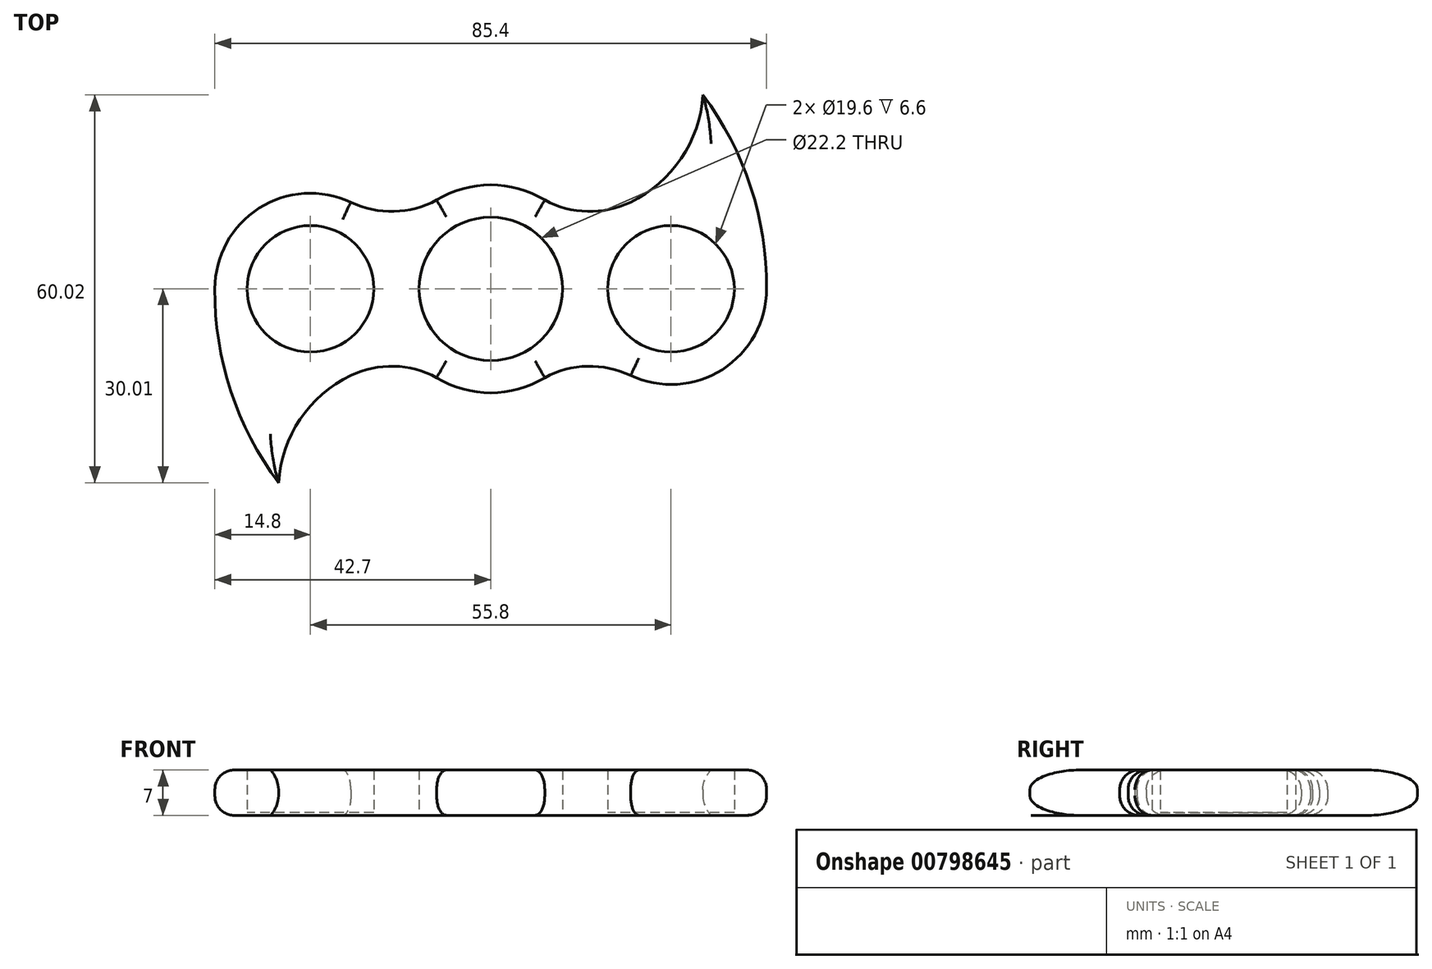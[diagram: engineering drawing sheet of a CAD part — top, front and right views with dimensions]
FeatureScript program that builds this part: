
annotation { "Feature Type Name" : "Feature", "Feature Type Description" : "" }
export const myFeature = defineFeature(function(context is Context, id is Id, definition is map)
    precondition{}
    {
        {
            var Q0;
            Q0=qCreatedBy(makeId("Top.planeOp"),FACE);
            var sketch = newSketch(context, id + "F0", { "sketchPlane" : qUnion([Q0])});
            skCircle(sketch, "E0", {"center": v(0, 0) * mm, "radius": 11.1 * mm});
            skCircle(sketch, "E1", {"center": v(27.9, 0) * mm, "radius": 9.8 * mm});
            skPoint(sketch, "E2", {"position": v(11.1, 0) * mm});
            skPoint(sketch, "E3", {"position": v(18.1, 0) * mm});
            skArc(sketch, "E4.0", {"start": v(21.5, -13.35) * mm, "mid": v(35.79, -12.52) * mm, "end": v(42.7, 0) * mm});
            skArc(sketch, "E5.0", {"start": v(-8.37, -13.76) * mm, "mid": v(0, -16.1) * mm, "end": v(8.37, -13.76) * mm});
            skArc(sketch, "E6", {"start": v(8.37, 13.76) * mm, "mid": v(14.97, 11.99) * mm, "end": v(21.65, 13.42) * mm});
            skArc(sketch, "E7", {"start": v(21.65, 13.42) * mm, "mid": v(29.5, 20.2) * mm, "end": v(32.85, 30.01) * mm});
            skArc(sketch, "E8", {"start": v(42.7, 0) * mm, "mid": v(40.23, 15.81) * mm, "end": v(32.85, 30.01) * mm});
            skArc(sketch, "E9.MirrorCS", {"start": v(8.37, -13.76) * mm, "mid": v(14.97, -11.99) * mm, "end": v(21.65, -13.42) * mm});
            skCircle(sketch, "E10.1.0", {"center": v(-27.9, 0) * mm, "radius": 9.8 * mm});
            skArc(sketch, "E10.1.1", {"start": v(-21.5, 13.35) * mm, "mid": v(-35.79, 12.52) * mm, "end": v(-42.7, 0) * mm});
            skArc(sketch, "E10.1.2", {"start": v(-42.7, 0) * mm, "mid": v(-40.23, -15.81) * mm, "end": v(-32.85, -30.01) * mm});
            skArc(sketch, "E10.1.3", {"start": v(-21.65, -13.42) * mm, "mid": v(-29.5, -20.2) * mm, "end": v(-32.85, -30.01) * mm});
            skArc(sketch, "E10.1.4", {"start": v(-8.37, -13.76) * mm, "mid": v(-14.97, -11.99) * mm, "end": v(-21.65, -13.42) * mm});
            skArc(sketch, "E10.1.5", {"start": v(-8.37, 13.76) * mm, "mid": v(-14.97, 11.99) * mm, "end": v(-21.65, 13.42) * mm});
            skArc(sketch, "E11.trimOffspring", {"start": v(-21.65, -13.42) * mm, "mid": v(-21.58, -13.38) * mm, "end": v(-21.5, -13.35) * mm});
            skArc(sketch, "E12.trimOffspring", {"start": v(8.37, 13.76) * mm, "mid": v(0, 16.1) * mm, "end": v(-8.37, 13.76) * mm});
            skArc(sketch, "E13.trimOffspring", {"start": v(21.65, 13.42) * mm, "mid": v(21.58, 13.38) * mm, "end": v(21.5, 13.35) * mm});
            skSolve(sketch);
        }
        {
            var Q0;
            Q0=makeQuery(id+"F0.imprint","IMPRINT",FACE,{"disambiguationData":[TD([[makeQuery(id+"F0.imprint","IMPRINT",EDGE,{"derivedFrom":sQuery(id+"F0.wireOp",EDGE,"E0")}),-1.0]])]});
            extrude(context, id + "F1", {"entities" : qUnion([Q0]), "depth" : 7 * mm, "offsetDistance" : 25 * mm});
        }
        {
            var Q0;
            Q0=makeQuery(id+"F0.imprint","IMPRINT",FACE,{"disambiguationData":[TD([[makeQuery(id+"F0.imprint","IMPRINT",EDGE,{"derivedFrom":sQuery(id+"F0.wireOp",EDGE,"E10.1.0")}),1.0]])]});
            var Q1;
            Q1=makeQuery(id+"F0.imprint","IMPRINT",FACE,{"disambiguationData":[TD([[makeQuery(id+"F0.imprint","IMPRINT",EDGE,{"derivedFrom":sQuery(id+"F0.wireOp",EDGE,"E1")}),1.0]])]});
            extrude(context, id + "F2", {"entities" : qUnion([Q0, Q1]), "operationType" : NewBodyOperationType.ADD, "depth" : 0.4 * mm, "offsetDistance" : 25 * mm});
        }
        {
            var Q0;
            Q0=makeQuery(id+"F1.opExtrude","CAP_EDGE",EDGE,{"disambiguationData":[OSD([sQuery(id+"F0.wireOp",EDGE,"E10.1.2")])],"isStart":false});
            var Q1;
            Q1=makeQuery(id+"F1.opExtrude","CAP_EDGE",EDGE,{"disambiguationData":[OSD([sQuery(id+"F0.wireOp",EDGE,"E10.1.1")])],"isStart":false});
            var Q2;
            Q2=makeQuery(id+"F1.opExtrude","CAP_EDGE",EDGE,{"disambiguationData":[OSD([sQuery(id+"F0.wireOp",EDGE,"E10.1.5")])],"isStart":false});
            var Q3;
            Q3=makeQuery(id+"F1.opExtrude","CAP_EDGE",EDGE,{"disambiguationData":[OSD([sQuery(id+"F0.wireOp",EDGE,"E12.trimOffspring")])],"isStart":false});
            var Q4;
            Q4=makeQuery(id+"F1.opExtrude","CAP_EDGE",EDGE,{"disambiguationData":[OSD([sQuery(id+"F0.wireOp",EDGE,"E6")])],"isStart":false});
            var Q5;
            Q5=makeQuery(id+"F1.opExtrude","CAP_EDGE",EDGE,{"disambiguationData":[OSD([sQuery(id+"F0.wireOp",EDGE,"E7")])],"isStart":false});
            var Q6;
            Q6=makeQuery(id+"F1.opExtrude","CAP_EDGE",EDGE,{"disambiguationData":[OSD([sQuery(id+"F0.wireOp",EDGE,"E8")])],"isStart":false});
            var Q7;
            Q7=makeQuery(id+"F1.opExtrude","CAP_EDGE",EDGE,{"disambiguationData":[OSD([sQuery(id+"F0.wireOp",EDGE,"E4.0")])],"isStart":false});
            var Q8;
            Q8=makeQuery(id+"F1.opExtrude","CAP_EDGE",EDGE,{"disambiguationData":[OSD([sQuery(id+"F0.wireOp",EDGE,"E9.MirrorCS")])],"isStart":false});
            var Q9;
            Q9=makeQuery(id+"F1.opExtrude","CAP_EDGE",EDGE,{"disambiguationData":[OSD([sQuery(id+"F0.wireOp",EDGE,"E5.0")])],"isStart":false});
            var Q10;
            Q10=makeQuery(id+"F1.opExtrude","CAP_EDGE",EDGE,{"disambiguationData":[OSD([sQuery(id+"F0.wireOp",EDGE,"E10.1.4")])],"isStart":false});
            var Q11;
            Q11=makeQuery(id+"F1.opExtrude","CAP_EDGE",EDGE,{"disambiguationData":[OSD([sQuery(id+"F0.wireOp",EDGE,"E10.1.3")])],"isStart":false});
            var Q12;
            Q12=makeQuery(id+"F1.opExtrude","CAP_EDGE",EDGE,{"disambiguationData":[OSD([sQuery(id+"F0.wireOp",EDGE,"E4.0")])],"isStart":true});
            var Q13;
            Q13=makeQuery(id+"F1.opExtrude","CAP_EDGE",EDGE,{"disambiguationData":[OSD([sQuery(id+"F0.wireOp",EDGE,"E9.MirrorCS")])],"isStart":true});
            var Q14;
            Q14=makeQuery(id+"F1.opExtrude","CAP_EDGE",EDGE,{"disambiguationData":[OSD([sQuery(id+"F0.wireOp",EDGE,"E5.0")])],"isStart":true});
            var Q15;
            Q15=makeQuery(id+"F1.opExtrude","CAP_EDGE",EDGE,{"disambiguationData":[OSD([sQuery(id+"F0.wireOp",EDGE,"E10.1.4")])],"isStart":true});
            var Q16;
            Q16=makeQuery(id+"F1.opExtrude","CAP_EDGE",EDGE,{"disambiguationData":[OSD([sQuery(id+"F0.wireOp",EDGE,"E10.1.3")])],"isStart":true});
            var Q17;
            Q17=makeQuery(id+"F1.opExtrude","CAP_EDGE",EDGE,{"disambiguationData":[OSD([sQuery(id+"F0.wireOp",EDGE,"E10.1.1")])],"isStart":true});
            var Q18;
            Q18=makeQuery(id+"F1.opExtrude","CAP_EDGE",EDGE,{"disambiguationData":[OSD([sQuery(id+"F0.wireOp",EDGE,"E10.1.2")])],"isStart":true});
            var Q19;
            Q19=makeQuery(id+"F1.opExtrude","CAP_EDGE",EDGE,{"disambiguationData":[OSD([sQuery(id+"F0.wireOp",EDGE,"E10.1.5")])],"isStart":true});
            var Q20;
            Q20=makeQuery(id+"F1.opExtrude","CAP_EDGE",EDGE,{"disambiguationData":[OSD([sQuery(id+"F0.wireOp",EDGE,"E12.trimOffspring")])],"isStart":true});
            var Q21;
            Q21=makeQuery(id+"F1.opExtrude","CAP_EDGE",EDGE,{"disambiguationData":[OSD([sQuery(id+"F0.wireOp",EDGE,"E6")])],"isStart":true});
            var Q22;
            Q22=makeQuery(id+"F1.opExtrude","CAP_EDGE",EDGE,{"disambiguationData":[OSD([sQuery(id+"F0.wireOp",EDGE,"E7")])],"isStart":true});
            fillet(context, id + "F3", {"entities" : qUnion([Q0, Q1, Q2, Q3, Q4, Q5, Q6, Q7, Q8, Q9, Q10, Q11, Q12, Q13, Q14, Q15, Q16, Q17, Q18, Q19, Q20, Q21, Q22]), "radius" : 3 * mm, "tangentPropagation" : true, "allowEdgeOverflow" : false});
        }
    });
